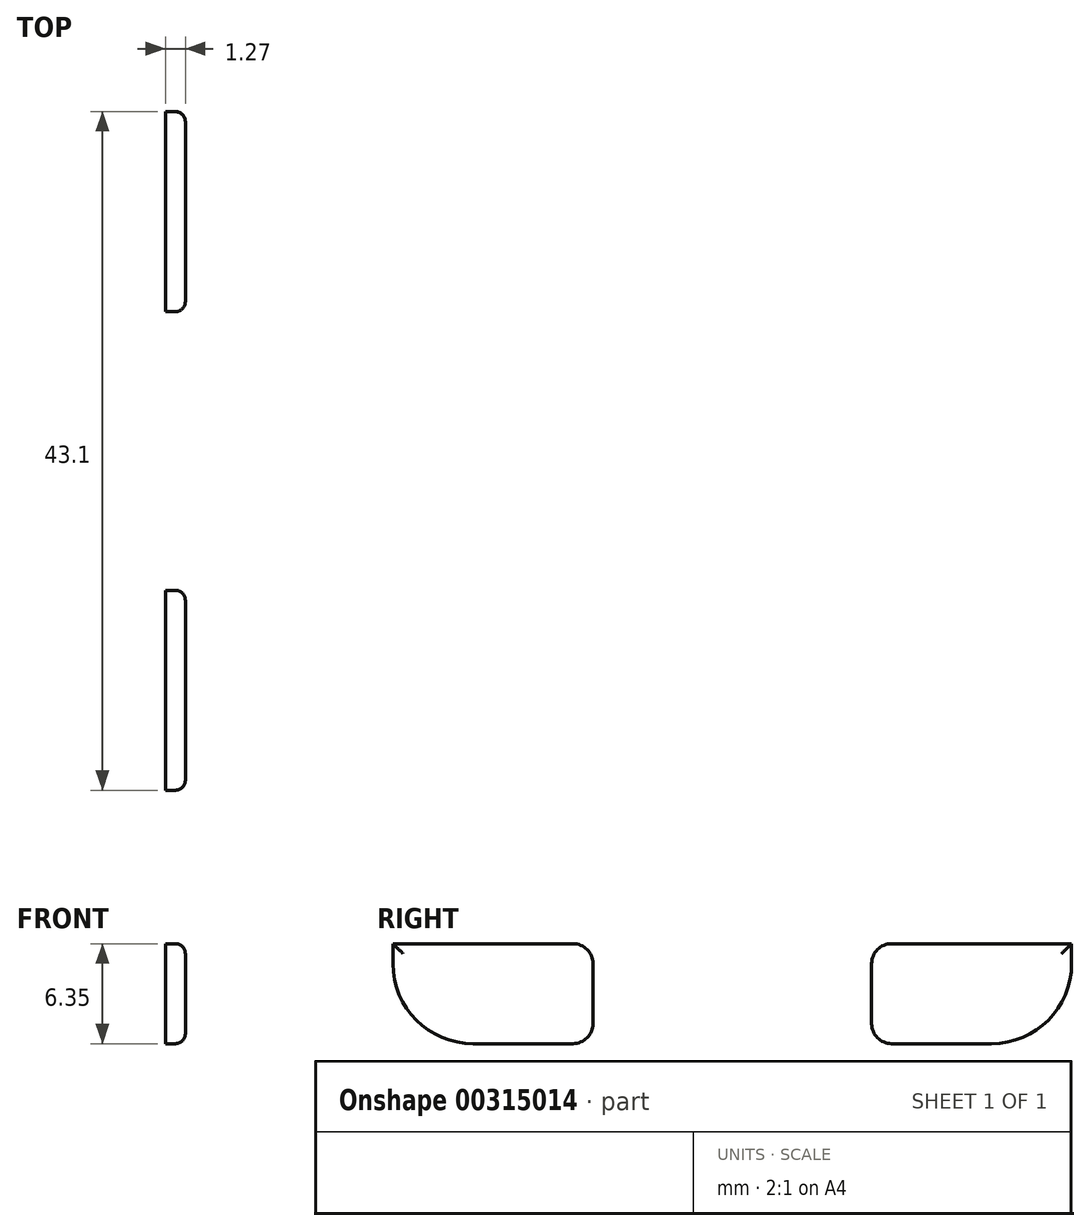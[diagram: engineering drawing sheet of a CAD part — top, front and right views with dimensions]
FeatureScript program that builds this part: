
annotation { "Feature Type Name" : "Feature", "Feature Type Description" : "" }
export const myFeature = defineFeature(function(context is Context, id is Id, definition is map)
    precondition{}
    {
        {
            var Q0;
            Q0=qCreatedBy(makeId("Right.planeOp"),FACE);
            var sketch = newSketch(context, id + "F0", { "sketchPlane" : qUnion([Q0])});
            skLineSegment(sketch, "E0.bottom", {"start": v(-37.77, 37.02) * mm, "end": v(-25.07, 37.02) * mm});
            skLineSegment(sketch, "E0.top", {"start": v(-37.77, 30.67) * mm, "end": v(-25.07, 30.67) * mm});
            skLineSegment(sketch, "E0.left", {"start": v(-37.77, 37.02) * mm, "end": v(-37.77, 30.67) * mm});
            skLineSegment(sketch, "E0.right", {"start": v(-25.07, 37.02) * mm, "end": v(-25.07, 30.67) * mm});
            skLineSegment(sketch, "E1.bottom", {"start": v(-7.37, 37.02) * mm, "end": v(5.33, 37.02) * mm});
            skLineSegment(sketch, "E1.top", {"start": v(-7.37, 30.67) * mm, "end": v(5.33, 30.67) * mm});
            skLineSegment(sketch, "E1.left", {"start": v(-7.37, 37.02) * mm, "end": v(-7.37, 30.67) * mm});
            skLineSegment(sketch, "E1.right", {"start": v(5.33, 37.02) * mm, "end": v(5.33, 30.67) * mm});
            skSolve(sketch);
        }
        {
            var Q0;
            Q0=makeQuery(id+"F0.imprint","IMPRINT",FACE,{"disambiguationData":[TD([[makeQuery(id+"F0.imprint","IMPRINT",EDGE,{"derivedFrom":sQuery(id+"F0.wireOp",EDGE,"E0.bottom")}),-1.0]])]});
            var Q1;
            Q1=makeQuery(id+"F0.imprint","IMPRINT",FACE,{"disambiguationData":[TD([[makeQuery(id+"F0.imprint","IMPRINT",EDGE,{"derivedFrom":sQuery(id+"F0.wireOp",EDGE,"E1.bottom")}),-1.0]])]});
            extrude(context, id + "F1", {"entities" : qUnion([Q0, Q1]), "depth" : 1.27 * mm});
        }
        {
            var Q0;
            Q0=makeQuery(id+"F1.opExtrude","CAP_EDGE",EDGE,{"disambiguationData":[OSD([sQuery(id+"F0.wireOp",EDGE,"E0.bottom")])],"isStart":false});
            var Q1;
            Q1=makeQuery(id+"F1.opExtrude","CAP_EDGE",EDGE,{"disambiguationData":[OSD([sQuery(id+"F0.wireOp",EDGE,"E0.right")])],"isStart":false});
            var Q2;
            Q2=makeQuery(id+"F1.opExtrude","CAP_EDGE",EDGE,{"disambiguationData":[OSD([sQuery(id+"F0.wireOp",EDGE,"E0.top")])],"isStart":false});
            var Q3;
            Q3=makeQuery(id+"F1.opExtrude","CAP_EDGE",EDGE,{"disambiguationData":[OSD([sQuery(id+"F0.wireOp",EDGE,"E0.left")])],"isStart":false});
            var Q4;
            Q4=makeQuery(id+"F1.opExtrude","CAP_EDGE",EDGE,{"disambiguationData":[OSD([sQuery(id+"F0.wireOp",EDGE,"E1.bottom")])],"isStart":false});
            var Q5;
            Q5=makeQuery(id+"F1.opExtrude","CAP_EDGE",EDGE,{"disambiguationData":[OSD([sQuery(id+"F0.wireOp",EDGE,"E1.left")])],"isStart":false});
            var Q6;
            Q6=makeQuery(id+"F1.opExtrude","CAP_EDGE",EDGE,{"disambiguationData":[OSD([sQuery(id+"F0.wireOp",EDGE,"E1.top")])],"isStart":false});
            var Q7;
            Q7=makeQuery(id+"F1.opExtrude","CAP_EDGE",EDGE,{"disambiguationData":[OSD([sQuery(id+"F0.wireOp",EDGE,"E1.right")])],"isStart":false});
            fillet(context, id + "F2", {"entities" : qUnion([Q0, Q1, Q2, Q3, Q4, Q5, Q6, Q7]), "radius" : 0.64 * mm, "tangentPropagation" : true, "allowEdgeOverflow" : false});
        }
        {
            var Q0;
            Q0=makeQuery(id+"F1.opExtrude","SWEPT_EDGE",EDGE,{"disambiguationData":[OSD([sQuery(id+"F0.wireOp",EDGE,"E1.top"),sQuery(id+"F0.wireOp",EDGE,"E1.right")])]});
            fillet(context, id + "F3", {"entities" : qUnion([Q0]), "radius" : 5.08 * mm, "tangentPropagation" : true, "allowEdgeOverflow" : false});
        }
        {
            var Q0;
            Q0=makeQuery(id+"F1.opExtrude","SWEPT_EDGE",EDGE,{"disambiguationData":[OSD([sQuery(id+"F0.wireOp",EDGE,"E0.top"),sQuery(id+"F0.wireOp",EDGE,"E0.left")])]});
            fillet(context, id + "F4", {"entities" : qUnion([Q0]), "radius" : 5.08 * mm, "tangentPropagation" : true, "allowEdgeOverflow" : false});
        }
        {
            var Q0;
            Q0=makeQuery(id+"F1.opExtrude","SWEPT_EDGE",EDGE,{"disambiguationData":[OSD([sQuery(id+"F0.wireOp",EDGE,"E0.bottom"),sQuery(id+"F0.wireOp",EDGE,"E0.right")])]});
            fillet(context, id + "F5", {"entities" : qUnion([Q0]), "radius" : 1.27 * mm, "tangentPropagation" : true, "allowEdgeOverflow" : false});
        }
        {
            var Q0;
            Q0=makeQuery(id+"F1.opExtrude","SWEPT_EDGE",EDGE,{"disambiguationData":[OSD([sQuery(id+"F0.wireOp",EDGE,"E1.bottom"),sQuery(id+"F0.wireOp",EDGE,"E1.left")])]});
            fillet(context, id + "F6", {"entities" : qUnion([Q0]), "radius" : 1.27 * mm, "tangentPropagation" : true, "allowEdgeOverflow" : false});
        }
        {
            var Q0;
            Q0=makeQuery(id+"F1.opExtrude","SWEPT_EDGE",EDGE,{"disambiguationData":[OSD([sQuery(id+"F0.wireOp",EDGE,"E0.top"),sQuery(id+"F0.wireOp",EDGE,"E0.right")])]});
            fillet(context, id + "F7", {"entities" : qUnion([Q0]), "radius" : 1.27 * mm, "tangentPropagation" : true, "allowEdgeOverflow" : false});
        }
        {
            var Q0;
            Q0=makeQuery(id+"F1.opExtrude","SWEPT_EDGE",EDGE,{"disambiguationData":[OSD([sQuery(id+"F0.wireOp",EDGE,"E1.top"),sQuery(id+"F0.wireOp",EDGE,"E1.left")])]});
            fillet(context, id + "F8", {"entities" : qUnion([Q0]), "radius" : 1.27 * mm, "tangentPropagation" : true, "allowEdgeOverflow" : false});
        }
    });
